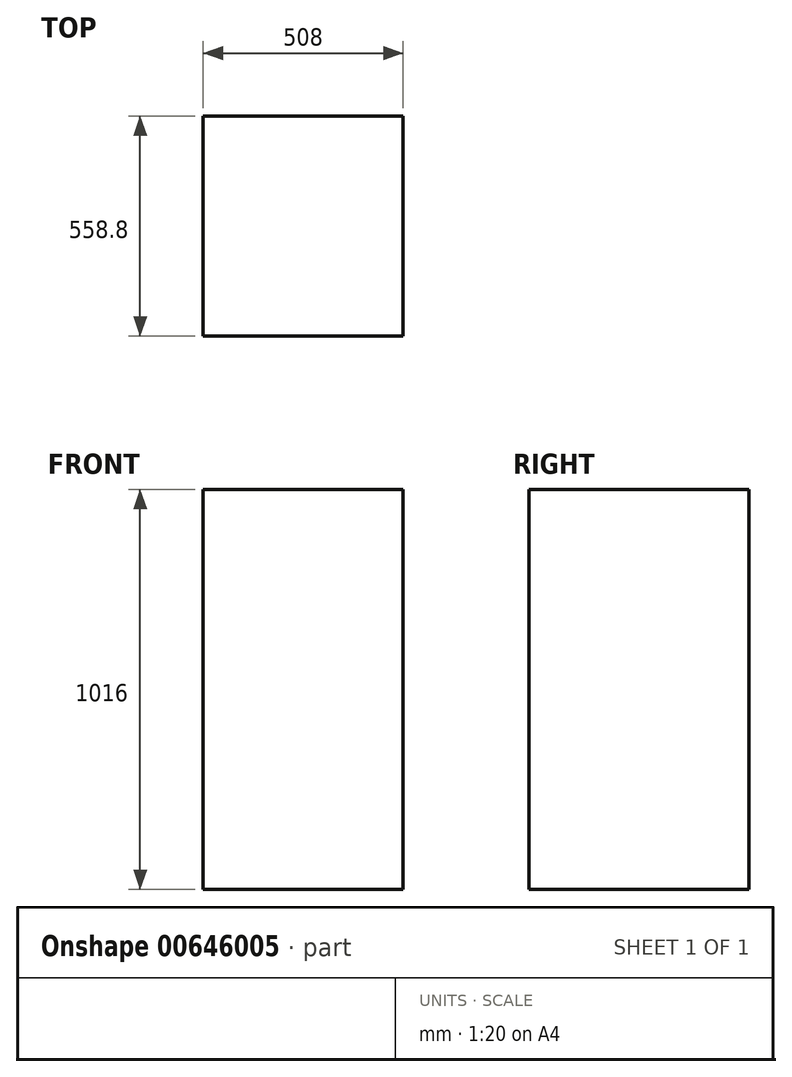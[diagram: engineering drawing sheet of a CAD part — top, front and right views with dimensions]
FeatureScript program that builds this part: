
annotation { "Feature Type Name" : "Feature", "Feature Type Description" : "" }
export const myFeature = defineFeature(function(context is Context, id is Id, definition is map)
    precondition{}
    {
        {
            var Q0;
            Q0=qCreatedBy(makeId("Top.planeOp"),FACE);
            var sketch = newSketch(context, id + "F0", { "sketchPlane" : qUnion([Q0])});
            skLineSegment(sketch, "E0.bottom", {"start": v(254, 279.4) * mm, "end": v(-254, 279.4) * mm});
            skLineSegment(sketch, "E0.top", {"start": v(254, -279.4) * mm, "end": v(-254, -279.4) * mm});
            skLineSegment(sketch, "E0.left", {"start": v(254, 279.4) * mm, "end": v(254, -279.4) * mm});
            skLineSegment(sketch, "E0.right", {"start": v(-254, 279.4) * mm, "end": v(-254, -279.4) * mm});
            skPoint(sketch, "E0.middle", {"position": v(0, 0) * mm});
            skSolve(sketch);
        }
        {
            var Q0;
            Q0=makeQuery(id+"F0.imprint","IMPRINT",FACE,{"disambiguationData":[TD([[makeQuery(id+"F0.imprint","IMPRINT",EDGE,{"derivedFrom":sQuery(id+"F0.wireOp",EDGE,"E0.bottom")}),1.0]])]});
            extrude(context, id + "F1", {"entities" : qUnion([Q0]), "depth" : 1016 * mm, "offsetDistance" : 25.4 * mm});
        }
    });
